# Revit family: Access_Door-Roof_Hatch-Cendrex-TRH
name_source: partatom
category: Specialty Equipment
revit_build: Autodesk Revit Architecture 2013 (Build: 20130531_2115(x64)
units: mm (PartAtom-declared; Revit-internal decimal feet)

## types (3) — shared parameters
Assembly Code = C1020700
Available Options = http://cendrex.com
Cendrex LEED Ready Program = http://www.cendrex.com
Construction Material = Metal - Cendrex - Aluminum
Default Elevation = 0"
Description = Roof hatch
Finish = Metal - Cendrex - Powder Coated White
Height = 12"
Manufacturer = Cendrex
Model = TRH
Product Documentation Link = http://cendrex.com
Product Page URL = http://cendrex.com
URL = http://www.cendrex.com

## per-type parameters (varying)
| type | Door Height | Door Width | Frame Height | Frame Width |
| Custom | 48" | 48" | 49 11/32" | 49 29/32" |
| 36 x 30 | 30" | 36" | 31 11/32" | 37 29/32" |
| 36 x 36 | 36" | 36" | 37 11/32" | 37 29/32" |

## geometry (parser evidence)
native form markers: Blend x15, Sweep x9
no freeform markers — native parametric forms only
